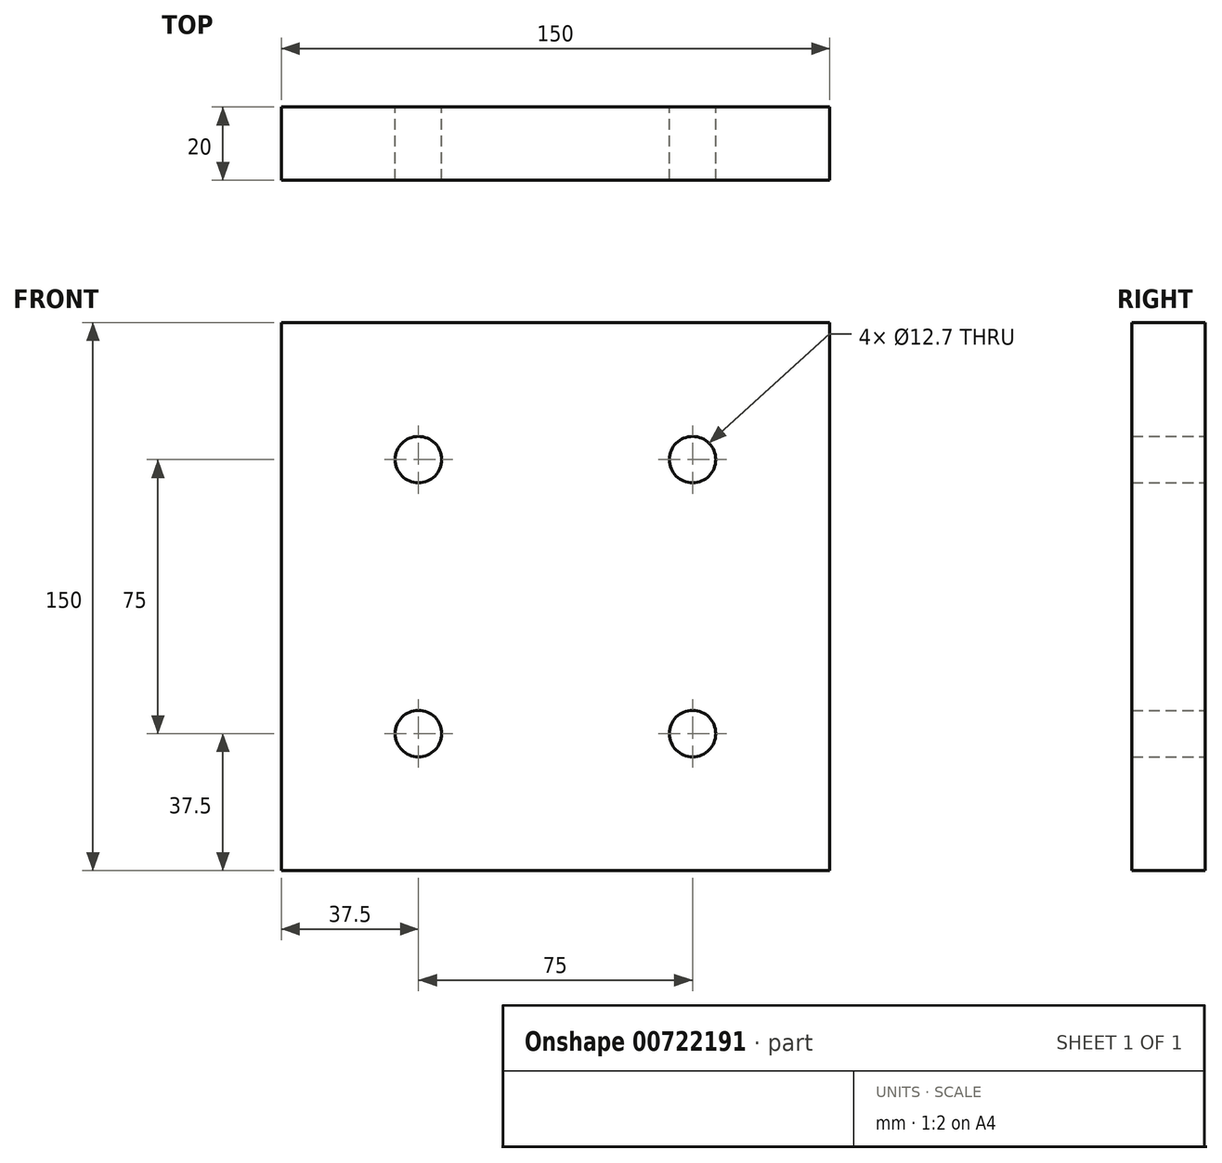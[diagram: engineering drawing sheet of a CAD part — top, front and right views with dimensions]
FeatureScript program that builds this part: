
annotation { "Feature Type Name" : "Feature", "Feature Type Description" : "" }
export const myFeature = defineFeature(function(context is Context, id is Id, definition is map)
    precondition{}
    {
        {
            var Q0;
            Q0=qCreatedBy(makeId("Front.planeOp"),FACE);
            var sketch = newSketch(context, id + "F0", { "sketchPlane" : qUnion([Q0])});
            skLineSegment(sketch, "E0.bottom", {"start": v(75, 75) * mm, "end": v(-75, 75) * mm});
            skLineSegment(sketch, "E0.top", {"start": v(75, -75) * mm, "end": v(-75, -75) * mm});
            skLineSegment(sketch, "E0.left", {"start": v(75, 75) * mm, "end": v(75, -75) * mm});
            skLineSegment(sketch, "E0.right", {"start": v(-75, 75) * mm, "end": v(-75, -75) * mm});
            skPoint(sketch, "E0.middle", {"position": v(0, 0) * mm});
            skCircle(sketch, "E1", {"center": v(-37.5, 37.5) * mm, "radius": 6.35 * mm});
            skCircle(sketch, "E2", {"center": v(37.5, 37.5) * mm, "radius": 6.35 * mm});
            skCircle(sketch, "E3", {"center": v(37.5, -37.5) * mm, "radius": 6.35 * mm});
            skCircle(sketch, "E4", {"center": v(-37.5, -37.5) * mm, "radius": 6.35 * mm});
            skSolve(sketch);
        }
        {
            var Q0;
            Q0=makeQuery(id+"F0.imprint","IMPRINT",FACE,{"disambiguationData":[TD([[makeQuery(id+"F0.imprint","IMPRINT",EDGE,{"derivedFrom":sQuery(id+"F0.wireOp",EDGE,"E0.bottom")}),1.0]])]});
            extrude(context, id + "F1", {"entities" : qUnion([Q0]), "depth" : 20 * mm, "offsetDistance" : 25 * mm});
        }
    });
